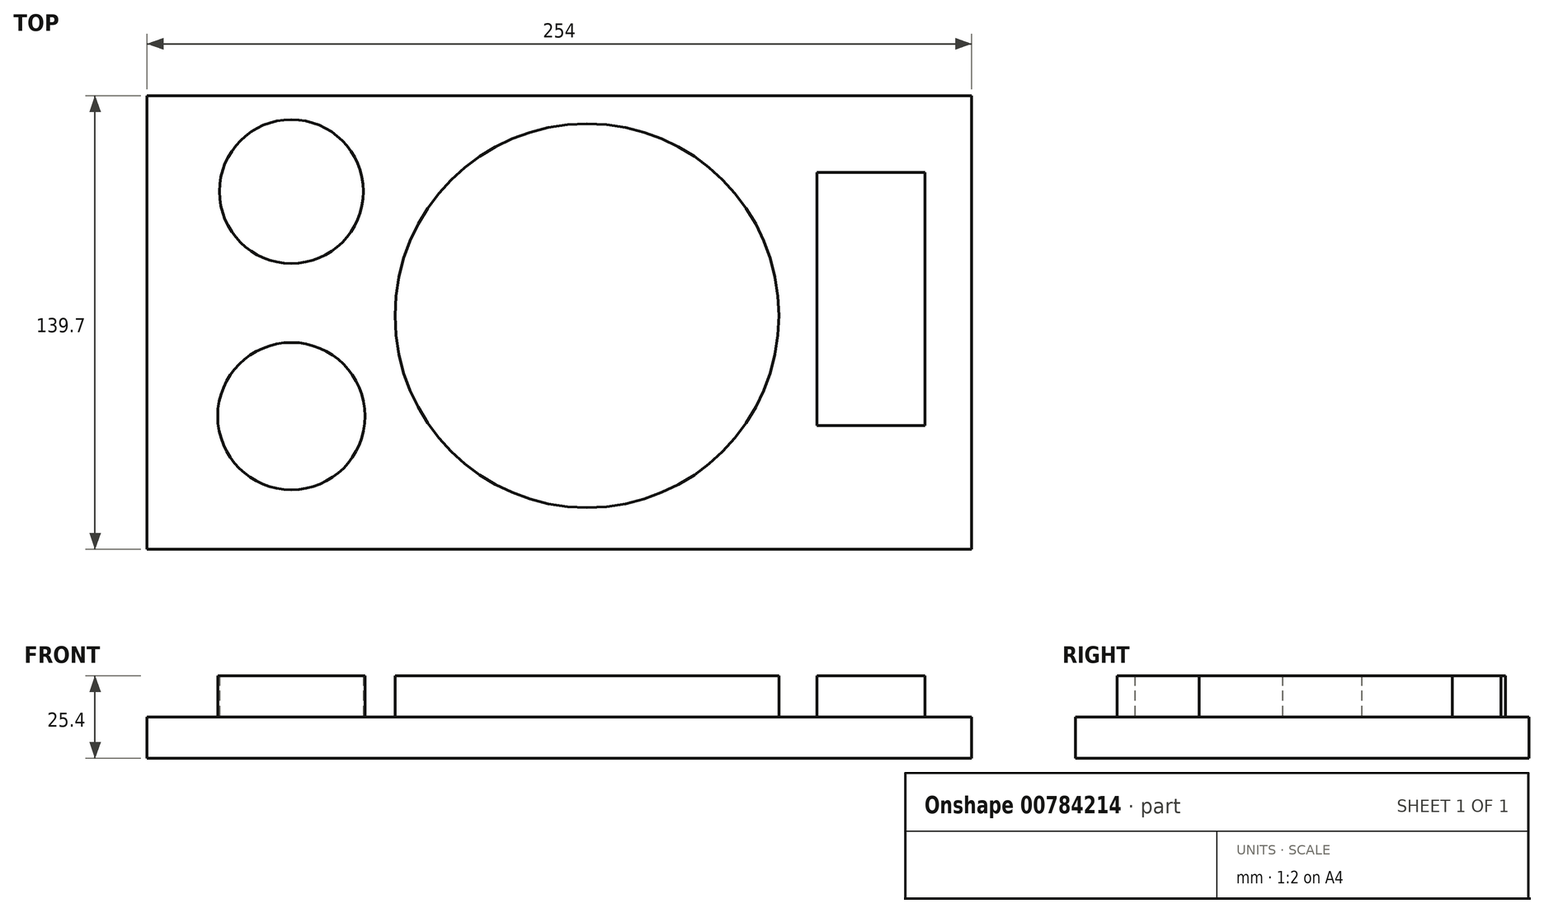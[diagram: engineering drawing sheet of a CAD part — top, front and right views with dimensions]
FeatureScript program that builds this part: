
annotation { "Feature Type Name" : "Feature", "Feature Type Description" : "" }
export const myFeature = defineFeature(function(context is Context, id is Id, definition is map)
    precondition{}
    {
        {
            var Q0;
            Q0=qCreatedBy(makeId("Top.planeOp"),FACE);
            var sketch = newSketch(context, id + "F0", { "sketchPlane" : qUnion([Q0])});
            skLineSegment(sketch, "E0.bottom", {"start": v(-123.2, 67.75) * mm, "end": v(130.8, 67.75) * mm});
            skLineSegment(sketch, "E0.top", {"start": v(-123.2, -71.95) * mm, "end": v(130.8, -71.95) * mm});
            skLineSegment(sketch, "E0.left", {"start": v(-123.2, 67.75) * mm, "end": v(-123.2, -71.95) * mm});
            skLineSegment(sketch, "E0.right", {"start": v(130.8, 67.75) * mm, "end": v(130.8, -71.95) * mm});
            skSolve(sketch);
        }
        {
            var Q0;
            Q0=makeQuery(id+"F0.imprint","IMPRINT",FACE,{"disambiguationData":[TD([[makeQuery(id+"F0.imprint","IMPRINT",EDGE,{"derivedFrom":sQuery(id+"F0.wireOp",EDGE,"E0.bottom")}),-1.0]])]});
            extrude(context, id + "F1", {"entities" : qUnion([Q0]), "depth" : 12.7 * mm, "offsetDistance" : 25.4 * mm});
        }
        {
            var Q0;
            Q0=makeQuery(id+"F1.opExtrude","CAP_FACE",FACE,{"disambiguationData":[OSD([sQuery(id+"F0.wireOp",EDGE,"E0.bottom"),sQuery(id+"F0.wireOp",EDGE,"E0.top"),sQuery(id+"F0.wireOp",EDGE,"E0.left"),sQuery(id+"F0.wireOp",EDGE,"E0.right")])],"isStart":false});
            var sketch = newSketch(context, id + "F2", { "sketchPlane" : qUnion([Q0])});
            skCircle(sketch, "E1", {"center": v(12.29, 0) * mm, "radius": 59.13 * mm});
            skCircle(sketch, "E2", {"center": v(-78.76, 38.27) * mm, "radius": 22.16 * mm});
            skCircle(sketch, "E3", {"center": v(-78.76, -30.96) * mm, "radius": 22.7 * mm});
            skLineSegment(sketch, "E4.bottom", {"start": v(83.13, 44.12) * mm, "end": v(116.37, 44.12) * mm});
            skLineSegment(sketch, "E4.top", {"start": v(83.13, -33.9) * mm, "end": v(116.37, -33.9) * mm});
            skLineSegment(sketch, "E4.left", {"start": v(83.13, 44.12) * mm, "end": v(83.13, -33.9) * mm});
            skLineSegment(sketch, "E4.right", {"start": v(116.37, 44.12) * mm, "end": v(116.37, -33.9) * mm});
            skSolve(sketch);
        }
        {
            var Q0;
            Q0=makeQuery(id+"F2.imprint","IMPRINT",FACE,{"disambiguationData":[TD([[makeQuery(id+"F2.imprint","IMPRINT",EDGE,{"derivedFrom":sQuery(id+"F2.wireOp",EDGE,"E2")}),1.0]])]});
            var Q1;
            Q1=makeQuery(id+"F2.imprint","IMPRINT",FACE,{"disambiguationData":[TD([[makeQuery(id+"F2.imprint","IMPRINT",EDGE,{"derivedFrom":sQuery(id+"F2.wireOp",EDGE,"E3")}),1.0]])]});
            var Q2;
            Q2=makeQuery(id+"F2.imprint","IMPRINT",FACE,{"disambiguationData":[TD([[makeQuery(id+"F2.imprint","IMPRINT",EDGE,{"derivedFrom":sQuery(id+"F2.wireOp",EDGE,"E1")}),1.0]])]});
            var Q3;
            Q3=makeQuery(id+"F2.imprint","IMPRINT",FACE,{"disambiguationData":[TD([[makeQuery(id+"F2.imprint","IMPRINT",EDGE,{"derivedFrom":sQuery(id+"F2.wireOp",EDGE,"E4.bottom")}),-1.0]])]});
            extrude(context, id + "F3", {"entities" : qUnion([Q0, Q1, Q2, Q3]), "operationType" : NewBodyOperationType.ADD, "depth" : 12.7 * mm, "offsetDistance" : 25.4 * mm});
        }
    });
